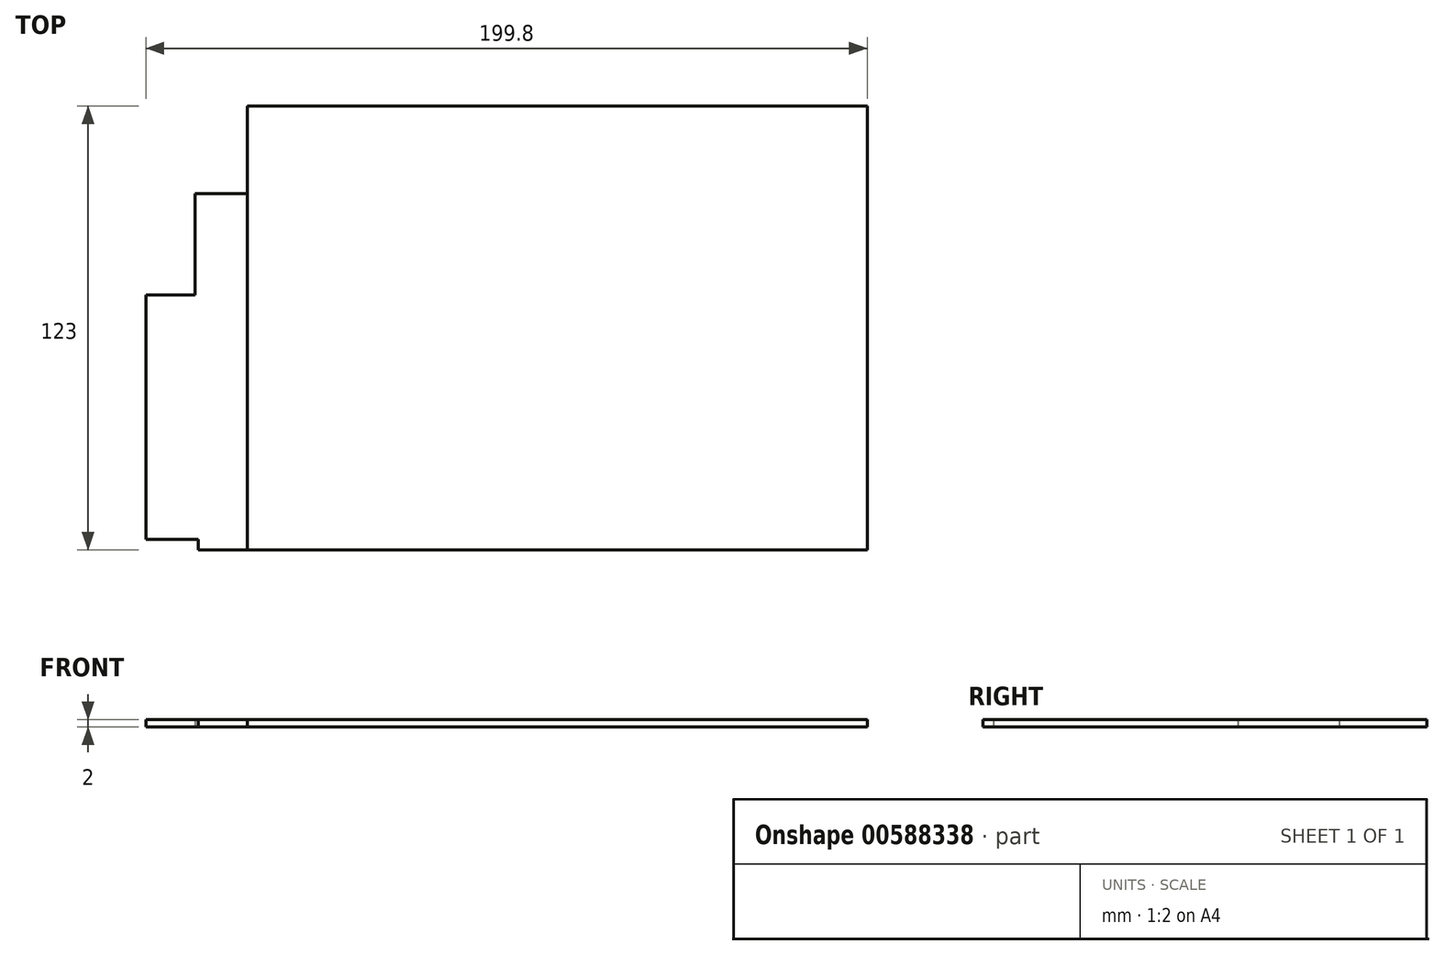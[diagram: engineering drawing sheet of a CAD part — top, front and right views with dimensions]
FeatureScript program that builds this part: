
annotation { "Feature Type Name" : "Feature", "Feature Type Description" : "" }
export const myFeature = defineFeature(function(context is Context, id is Id, definition is map)
    precondition{}
    {
        {
            var Q0;
            Q0=qCreatedBy(makeId("Top.planeOp"),FACE);
            var sketch = newSketch(context, id + "F0", { "sketchPlane" : qUnion([Q0])});
            skLineSegment(sketch, "E0.bottom", {"start": v(-98.68, 61.5) * mm, "end": v(72.97, 61.5) * mm});
            skLineSegment(sketch, "E0.top", {"start": v(-98.68, -38.5) * mm, "end": v(72.97, -38.5) * mm});
            skLineSegment(sketch, "E0.left", {"start": v(-98.68, 61.5) * mm, "end": v(-98.68, -38.5) * mm});
            skLineSegment(sketch, "E0.right", {"start": v(72.97, 61.5) * mm, "end": v(72.97, -38.5) * mm});
            skSolve(sketch);
        }
        {
            var Q0;
            Q0=makeQuery(id+"F0.imprint","IMPRINT",FACE,{"disambiguationData":[TD([[makeQuery(id+"F0.imprint","IMPRINT",EDGE,{"derivedFrom":sQuery(id+"F0.wireOp",EDGE,"E0.bottom")}),-1.0]])]});
            extrude(context, id + "F1", {"entities" : qUnion([Q0]), "depth" : 2 * mm, "offsetDistance" : 25 * mm});
        }
        {
            var Q0;
            Q0=makeQuery(id+"F1.opExtrude","SWEPT_FACE",FACE,{"disambiguationData":[OSD([sQuery(id+"F0.wireOp",EDGE,"E0.bottom")])]});
            extrude(context, id + "F2", {"entities" : qUnion([Q0]), "operationType" : NewBodyOperationType.ADD, "depth" : 23 * mm, "offsetDistance" : 25 * mm});
        }
        {
            var Q0;
            {var subQ0=sQuery(id+"F0.wireOp",EDGE,"E0.bottom");Q0=makeQuery(id+"F2.boolean.opBoolean","MERGE",FACE,{"derivedFrom":[makeQuery(id+"F1.opExtrude","CAP_FACE",FACE,{"disambiguationData":[OSD([subQ0,sQuery(id+"F0.wireOp",EDGE,"E0.top"),sQuery(id+"F0.wireOp",EDGE,"E0.left"),sQuery(id+"F0.wireOp",EDGE,"E0.right")])],"isStart":true}),makeQuery(id+"F2.opExtrude","SWEPT_FACE",FACE,{"disambiguationData":[OSD([subQ0]),TDD([makeQuery(id+"F1.opExtrude","CAP_EDGE",EDGE,{"disambiguationData":[OSD([subQ0])],"isStart":true})])]})]});}
            var sketch = newSketch(context, id + "F3", { "sketchPlane" : qUnion([Q0])});
            skLineSegment(sketch, "E1.0", {"start": v(-98.68, 38.5) * mm, "end": v(72.97, 38.5) * mm});
            skLineSegment(sketch, "E2.0", {"start": v(-98.68, -84.5) * mm, "end": v(-98.68, 38.5) * mm});
            skLineSegment(sketch, "E3", {"start": v(-98.68, 38.5) * mm, "end": v(-112.33, 38.5) * mm});
            skLineSegment(sketch, "E4", {"start": v(-112.33, 38.5) * mm, "end": v(-112.33, 35.5) * mm});
            skLineSegment(sketch, "E5", {"start": v(-112.33, 35.5) * mm, "end": v(-126.83, 35.5) * mm});
            skLineSegment(sketch, "E6", {"start": v(-98.68, -84.5) * mm, "end": v(-98.68, -60.2) * mm});
            skLineSegment(sketch, "E7", {"start": v(-98.68, -60.2) * mm, "end": v(-113.18, -60.2) * mm});
            skLineSegment(sketch, "E8", {"start": v(-113.18, -60.2) * mm, "end": v(-113.18, -32.2) * mm});
            skLineSegment(sketch, "E9", {"start": v(-113.18, -32.2) * mm, "end": v(-146.18, -32.2) * mm});
            skLineSegment(sketch, "E10", {"start": v(-146.18, -32.2) * mm, "end": v(-146.18, -60.2) * mm});
            skLineSegment(sketch, "E11", {"start": v(-126.83, 35.5) * mm, "end": v(-126.83, -32.2) * mm});
            skSolve(sketch);
        }
        {
            var Q0;
            Q0=makeQuery(id+"F3.imprint","IMPRINT",FACE,{"disambiguationData":[TD([[makeQuery(id+"F3.imprint","IMPRINT",EDGE,{"derivedFrom":sQuery(id+"F3.wireOp",EDGE,"E2.0")}),1.0]])]});
            extrude(context, id + "F4", {"entities" : qUnion([Q0]), "oppositeDirection" : true, "depth" : 2 * mm, "offsetDistance" : 25 * mm});
        }
    });
